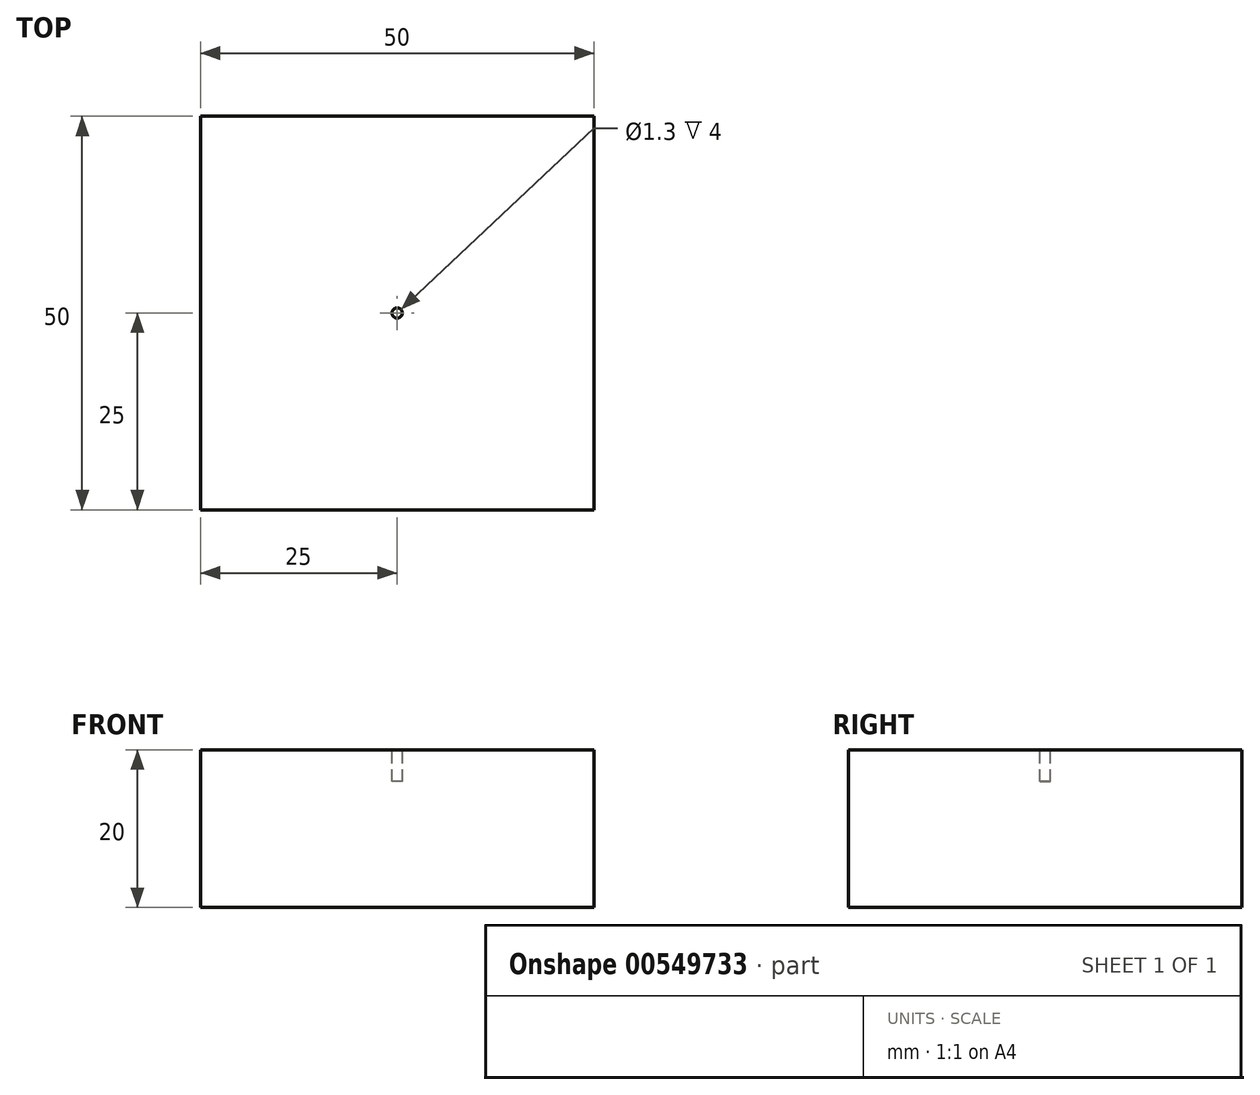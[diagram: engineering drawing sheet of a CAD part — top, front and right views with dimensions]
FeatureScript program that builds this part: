
annotation { "Feature Type Name" : "Feature", "Feature Type Description" : "" }
export const myFeature = defineFeature(function(context is Context, id is Id, definition is map)
    precondition{}
    {
        {
            var Q0;
            Q0=qCreatedBy(makeId("Top.planeOp"),FACE);
            var sketch = newSketch(context, id + "F0", { "sketchPlane" : qUnion([Q0])});
            skLineSegment(sketch, "E0.bottom", {"start": v(25, -25) * mm, "end": v(-25, -25) * mm});
            skLineSegment(sketch, "E0.top", {"start": v(25, 25) * mm, "end": v(-25, 25) * mm});
            skLineSegment(sketch, "E0.left", {"start": v(25, -25) * mm, "end": v(25, 25) * mm});
            skLineSegment(sketch, "E0.right", {"start": v(-25, -25) * mm, "end": v(-25, 25) * mm});
            skPoint(sketch, "E0.middle", {"position": v(0, 0) * mm});
            skSolve(sketch);
        }
        {
            var Q0;
            Q0 = qSketchRegion(id + "F0", true);
            extrude(context, id + "F1", {"entities" : qUnion([Q0]), "endBound" : BoundingType.SYMMETRIC, "depth" : 20 * mm, "offsetDistance" : 25 * mm});
        }
        {
            var Q0;
            Q0=makeQuery(id+"F1.opExtrude","CAP_FACE",FACE,{"disambiguationData":[OSD([sQuery(id+"F0.wireOp",EDGE,"E0.bottom"),sQuery(id+"F0.wireOp",EDGE,"E0.top"),sQuery(id+"F0.wireOp",EDGE,"E0.left"),sQuery(id+"F0.wireOp",EDGE,"E0.right")])],"isStart":false});
            var sketch = newSketch(context, id + "F2", { "sketchPlane" : qUnion([Q0])});
            skCircle(sketch, "E1", {"center": v(0, 0) * mm, "radius": 0.65 * mm});
            skSolve(sketch);
        }
        {
            var Q0;
            Q0 = qSketchRegion(id + "F2", true);
            extrude(context, id + "F3", {"entities" : qUnion([Q0]), "operationType" : NewBodyOperationType.REMOVE, "oppositeDirection" : true, "depth" : 4 * mm, "offsetDistance" : 25 * mm});
        }
    });
